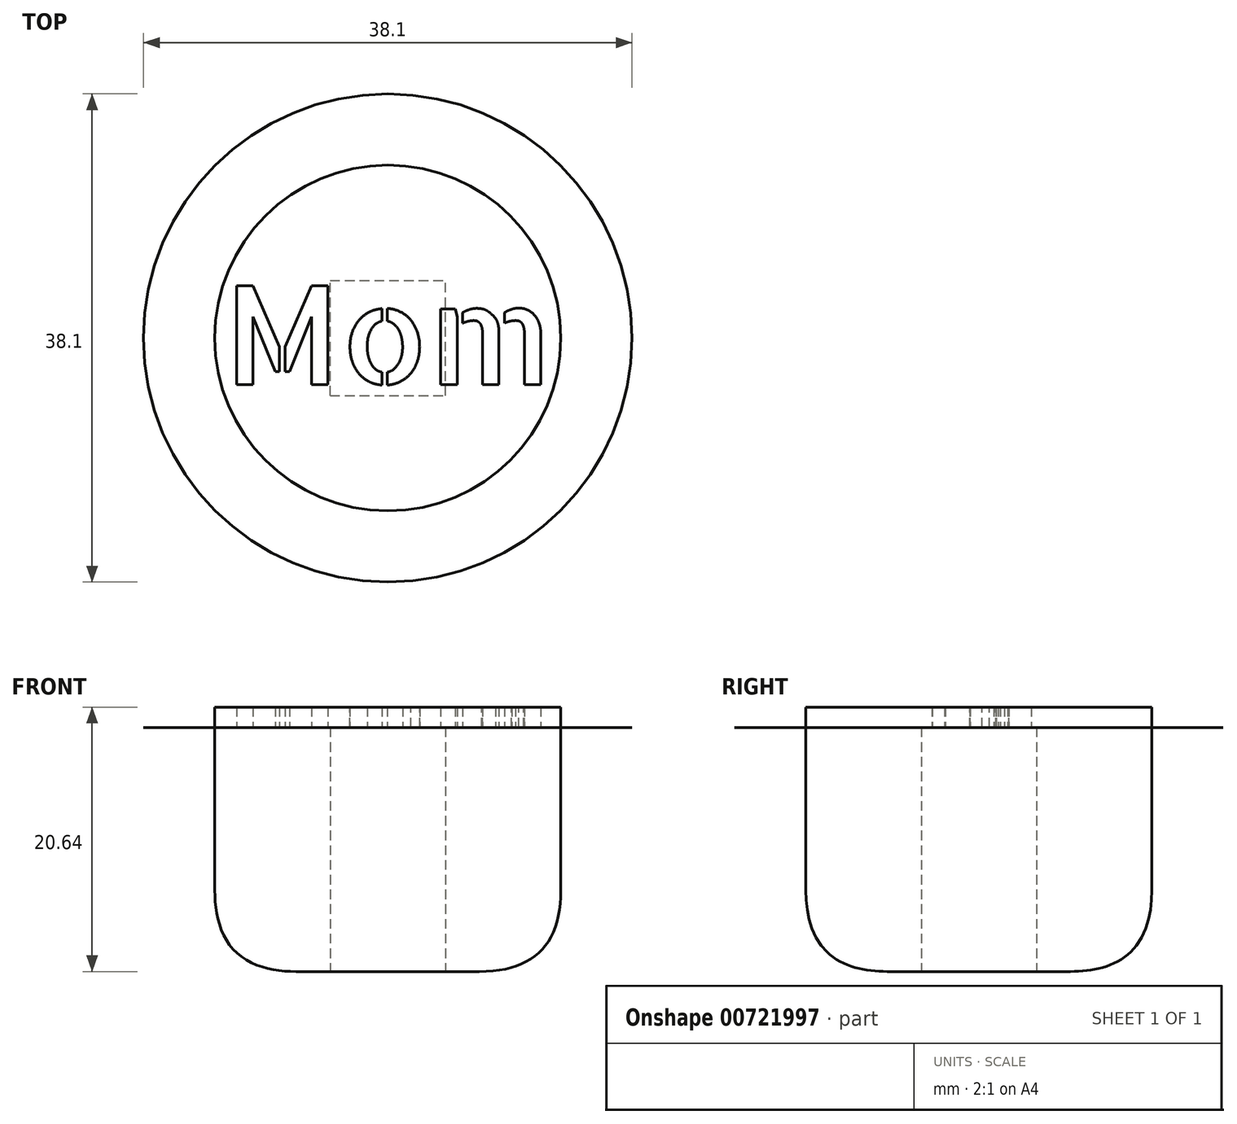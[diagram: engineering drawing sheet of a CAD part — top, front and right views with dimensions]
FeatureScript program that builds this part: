
annotation { "Feature Type Name" : "Feature", "Feature Type Description" : "" }
export const myFeature = defineFeature(function(context is Context, id is Id, definition is map)
    precondition{}
    {
        {
            var Q0;
            Q0=qCreatedBy(makeId("Top.planeOp"),FACE);
            var sketch = newSketch(context, id + "F0", { "sketchPlane" : qUnion([Q0])});
            skCircle(sketch, "E0", {"center": v(0, 0) * mm, "radius": 13.5 * mm});
            skText(sketch, "E1", { "text": "Mom", "fontName": "AllertaStencil-Regular.ttf"});
            const initialGuessF0  = {"E1": [-0.01276, -0.00363, 1, 0, 0.00772]};
            skSetInitialGuess(sketch, initialGuessF0);
            skSolve(sketch);
        }
        {
            var Q0;
            Q0=qCreatedBy(makeId("Top.planeOp"),FACE);
            var sketch = newSketch(context, id + "F1", { "sketchPlane" : qUnion([Q0])});
            skCircle(sketch, "E2", {"center": v(0, 0) * mm, "radius": 13.5 * mm});
            skSolve(sketch);
        }
        {
            var Q0;
            Q0 = qSketchRegion(id + "F0", true);
            extrude(context, id + "F2", {"entities" : qUnion([Q0]), "depth" : 1.59 * mm, "offsetDistance" : 25.4 * mm});
        }
        {
            var Q0;
            Q0 = qSketchRegion(id + "F1", true);
            extrude(context, id + "F3", {"entities" : qUnion([Q0]), "operationType" : NewBodyOperationType.ADD, "oppositeDirection" : true, "depth" : 19.05 * mm, "offsetDistance" : 25.4 * mm});
        }
        {
            var Q0;
            Q0=makeQuery(id+"F3.opExtrude","CAP_FACE",FACE,{"disambiguationData":[OSD([sQuery(id+"F1.wireOp",EDGE,"E2")])],"isStart":false});
            var sketch = newSketch(context, id + "F4", { "sketchPlane" : qUnion([Q0])});
            skLineSegment(sketch, "E3.bottom", {"start": v(-4.5, 4.5) * mm, "end": v(4.5, 4.5) * mm});
            skLineSegment(sketch, "E3.top", {"start": v(-4.5, -4.5) * mm, "end": v(4.5, -4.5) * mm});
            skLineSegment(sketch, "E3.left", {"start": v(-4.5, 4.5) * mm, "end": v(-4.5, -4.5) * mm});
            skLineSegment(sketch, "E3.right", {"start": v(4.5, 4.5) * mm, "end": v(4.5, -4.5) * mm});
            skPoint(sketch, "E3.middle", {"position": v(0, 0) * mm});
            skSolve(sketch);
        }
        {
            var Q0;
            Q0=makeQuery(id+"F3.opExtrude","CAP_EDGE",EDGE,{"disambiguationData":[OSD([sQuery(id+"F1.wireOp",EDGE,"E2")])],"isStart":false});
            fillet(context, id + "F5", {"entities" : qUnion([Q0]), "radius" : 6.35 * mm, "tangentPropagation" : true, "rho" : 0.5, "crossSection" : FilletCrossSection.CONIC, "allowEdgeOverflow" : false});
        }
        {
            var Q0;
            Q0 = qSketchRegion(id + "F4", true);
            extrude(context, id + "F6", {"entities" : qUnion([Q0]), "operationType" : NewBodyOperationType.REMOVE, "oppositeDirection" : true, "depth" : 19.05 * mm, "offsetDistance" : 25.4 * mm});
        }
        {
            var Q0;
            Q0=qCreatedBy(makeId("Top.planeOp"),FACE);
            var sketch = newSketch(context, id + "F7", { "sketchPlane" : qUnion([Q0])});
            skCircle(sketch, "E4", {"center": v(0, 0) * mm, "radius": 19.05 * mm});
            skSolve(sketch);
        }
        {
            var Q0;
            Q0 = qSketchRegion(id + "F7", true);
            extrude(context, id + "F8", {"entities" : qUnion([Q0]), "operationType" : NewBodyOperationType.ADD, "oppositeDirection" : true, "depth" : 1 / 203.2 * mm, "offsetDistance" : 25.4 * mm});
        }
        {
            var Q0;
            Q0=makeQuery(id+"F8.opExtrude","CAP_EDGE",EDGE,{"disambiguationData":[OSD([sQuery(id+"F7.wireOp",EDGE,"E4")])],"isStart":false});
            fillet(context, id + "F9", {"entities" : qUnion([Q0]), "radius" : 6.35 * mm, "tangentPropagation" : true, "allowEdgeOverflow" : false});
        }
    });
